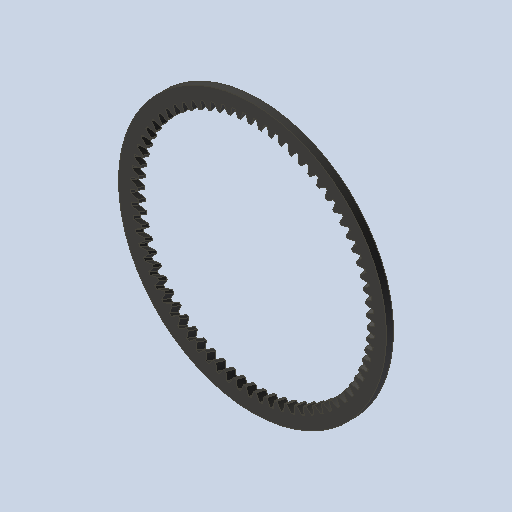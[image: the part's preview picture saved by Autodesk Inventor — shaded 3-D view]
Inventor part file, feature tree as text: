
AUTODESK INVENTOR PART (.ipt)
format: ipt  version: 2023 (Build 270158000, 158)  size: 880,128 bytes
history: native  units: mm (DEFAULTED — no unit token found)
features: plane x3, other x3, sketch x2, extrude x1
ambient origin geometry x8: Origin, YZ Plane, XZ Plane, XY Plane, X Axis, Y Axis, Z Axis, Center Point
bodies: Solid1 (feature_tree)
feature tree (9):
  extrude  "Extrusion1"  Depth=10.0mm TaperAngle=0.0deg
  plane  "Work Plane2"
  plane  "Work Plane8"
  plane  "Work Plane9"
  other  "Spur Gear"
  sketch  "Sketch1"  dims[d0=381.559759mm d1=10.0mm d2=0.0mm]
  sketch  "Sketch2"  dims[d3=335.215998mm d4=10.0mm d5=0.0mm d16=107.95mm d17=0.0mm d34=0.448799mm d39=0.0mm d45=0.0mm d47=107.95mm d50=0.0mm d51=0.0mm d52=107.95mm]
  other  "Srf1"
  other  "Pitch Diameter"
